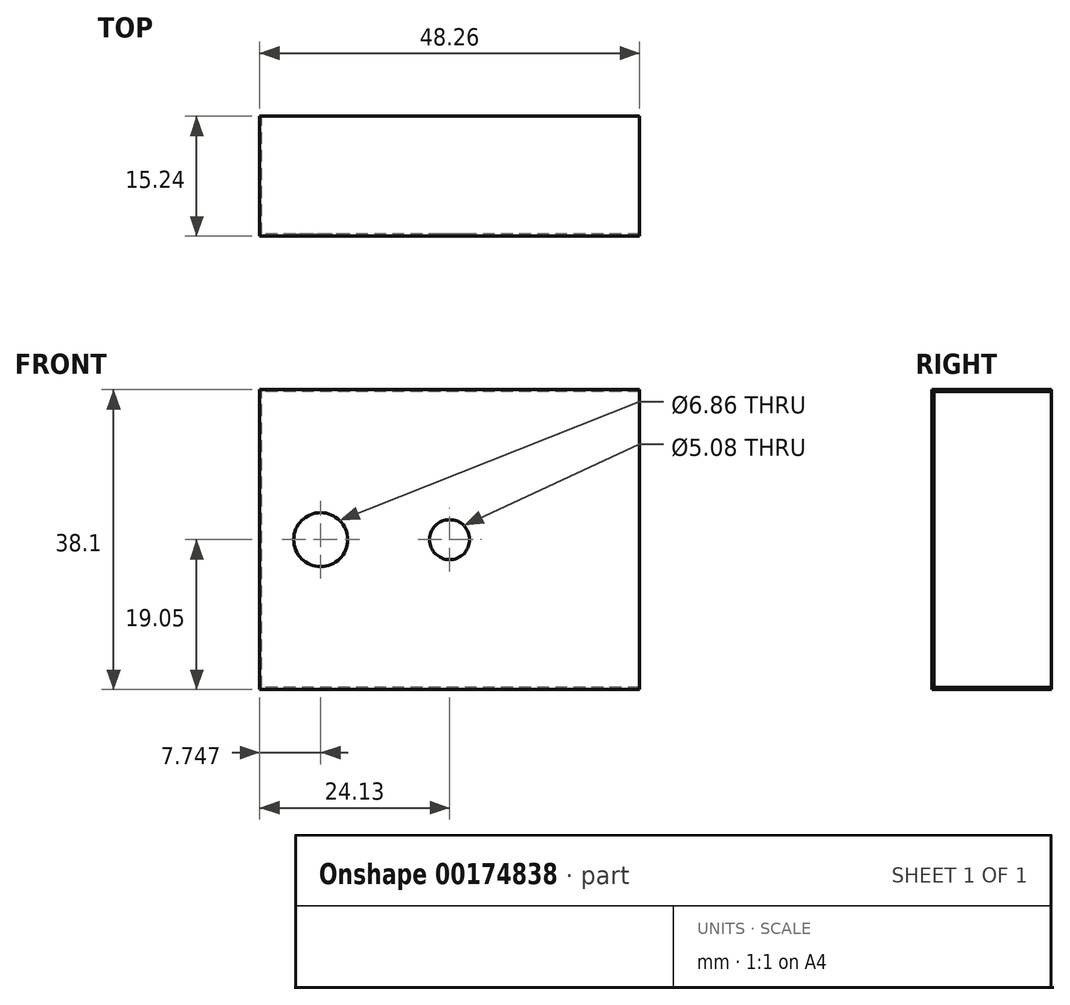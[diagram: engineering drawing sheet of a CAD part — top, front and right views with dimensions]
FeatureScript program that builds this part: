
annotation { "Feature Type Name" : "Feature", "Feature Type Description" : "" }
export const myFeature = defineFeature(function(context is Context, id is Id, definition is map)
    precondition{}
    {
        {
            var Q0;
            Q0=qCreatedBy(makeId("Front.planeOp"),FACE);
            var sketch = newSketch(context, id + "F0", { "sketchPlane" : qUnion([Q0])});
            skLineSegment(sketch, "E0.bottom", {"start": v(24.13, -19.05) * mm, "end": v(-24.13, -19.05) * mm});
            skLineSegment(sketch, "E0.top", {"start": v(24.13, 19.05) * mm, "end": v(-24.13, 19.05) * mm});
            skLineSegment(sketch, "E0.left", {"start": v(24.13, -19.05) * mm, "end": v(24.13, 19.05) * mm});
            skLineSegment(sketch, "E0.right", {"start": v(-24.13, -19.05) * mm, "end": v(-24.13, 19.05) * mm});
            skPoint(sketch, "E0.middle", {"position": v(0, 0) * mm});
            skSolve(sketch);
        }
        {
            var Q0;
            Q0=makeQuery(id+"F0.imprint","IMPRINT",FACE,{"disambiguationData":[TD([[makeQuery(id+"F0.imprint","IMPRINT",EDGE,{"derivedFrom":sQuery(id+"F0.wireOp",EDGE,"E0.bottom")}),-1.0]])]});
            extrude(context, id + "F1", {"entities" : qUnion([Q0]), "depth" : 15.24 * mm});
        }
        {
            var Q0;
            Q0=makeQuery(id+"F1.opExtrude","CAP_FACE",FACE,{"disambiguationData":[OSD([sQuery(id+"F0.wireOp",EDGE,"E0.bottom"),sQuery(id+"F0.wireOp",EDGE,"E0.top"),sQuery(id+"F0.wireOp",EDGE,"E0.left"),sQuery(id+"F0.wireOp",EDGE,"E0.right")])],"isStart":false});
            var sketch = newSketch(context, id + "F2", { "sketchPlane" : qUnion([Q0])});
            skLineSegment(sketch, "E1", {"start": v(-24.13, 2.53) * mm, "end": v(-19.81, 2.53) * mm});
            skLineSegment(sketch, "E2", {"start": v(-24.13, 0) * mm, "end": v(-16.38, 0) * mm});
            skPoint(sketch, "E2.endSnap0", {"position": v(-24.13, 0) * mm});
            skPoint(sketch, "E3.middle", {"position": v(-16.38, 0) * mm});
            skCircle(sketch, "E4", {"center": v(-16.38, 0) * mm, "radius": 3.43 * mm});
            skSolve(sketch);
        }
        {
            var Q0;
            Q0=makeQuery(id+"F1.opExtrude","CAP_FACE",FACE,{"disambiguationData":[OSD([sQuery(id+"F0.wireOp",EDGE,"E0.bottom"),sQuery(id+"F0.wireOp",EDGE,"E0.top"),sQuery(id+"F0.wireOp",EDGE,"E0.left"),sQuery(id+"F0.wireOp",EDGE,"E0.right")])],"isStart":true});
            var Q1;
            Q1=makeQuery(id+"F1.opExtrude","SWEPT_FACE",FACE,{"disambiguationData":[OSD([sQuery(id+"F0.wireOp",EDGE,"E0.left")])]});
            shell(context, id + "F3", {"entities" : qUnion([Q0, Q1]), "thickness" : 0.25 * mm});
        }
        {
            var Q0;
            Q0=sQuery(id+"F2.wireOp",VERTEX,"E3.middle");
            var Q1;
            Q1=makeQuery(id+"F1.opExtrude","SWEPT_BODY",BODY,{"disambiguationData":[OSD([sQuery(id+"F0.wireOp",EDGE,"E0.bottom"),sQuery(id+"F0.wireOp",EDGE,"E0.top"),sQuery(id+"F0.wireOp",EDGE,"E0.left"),sQuery(id+"F0.wireOp",EDGE,"E0.right")])]});
            hole(context, id + "F4", {"style" : HoleStyle.SIMPLE, "endStyle" : HoleEndStyle.THROUGH, "holeDiameter" : 6.86 * mm, "locations" : qUnion([Q0]), "scope" : qUnion([Q1]), "isTappedThrough" : true});
        }
        {
            var Q0;
            Q0=makeQuery(id+"F1.opExtrude","CAP_FACE",FACE,{"disambiguationData":[OSD([sQuery(id+"F0.wireOp",EDGE,"E0.bottom"),sQuery(id+"F0.wireOp",EDGE,"E0.top"),sQuery(id+"F0.wireOp",EDGE,"E0.left"),sQuery(id+"F0.wireOp",EDGE,"E0.right")])],"isStart":false});
            var sketch = newSketch(context, id + "F5", { "sketchPlane" : qUnion([Q0])});
            skCircle(sketch, "E5", {"center": v(0, 0) * mm, "radius": 2.54 * mm});
            skSolve(sketch);
        }
        {
            var Q0;
            Q0=sQuery(id+"F5.wireOp",VERTEX,"E5.center");
            var Q1;
            Q1=makeQuery(id+"F1.opExtrude","SWEPT_BODY",BODY,{"disambiguationData":[OSD([sQuery(id+"F0.wireOp",EDGE,"E0.bottom"),sQuery(id+"F0.wireOp",EDGE,"E0.top"),sQuery(id+"F0.wireOp",EDGE,"E0.left"),sQuery(id+"F0.wireOp",EDGE,"E0.right")])]});
            hole(context, id + "F6", {"style" : HoleStyle.SIMPLE, "endStyle" : HoleEndStyle.THROUGH, "holeDiameter" : 5.08 * mm, "locations" : qUnion([Q0]), "scope" : qUnion([Q1]), "isTappedThrough" : true});
        }
    });
